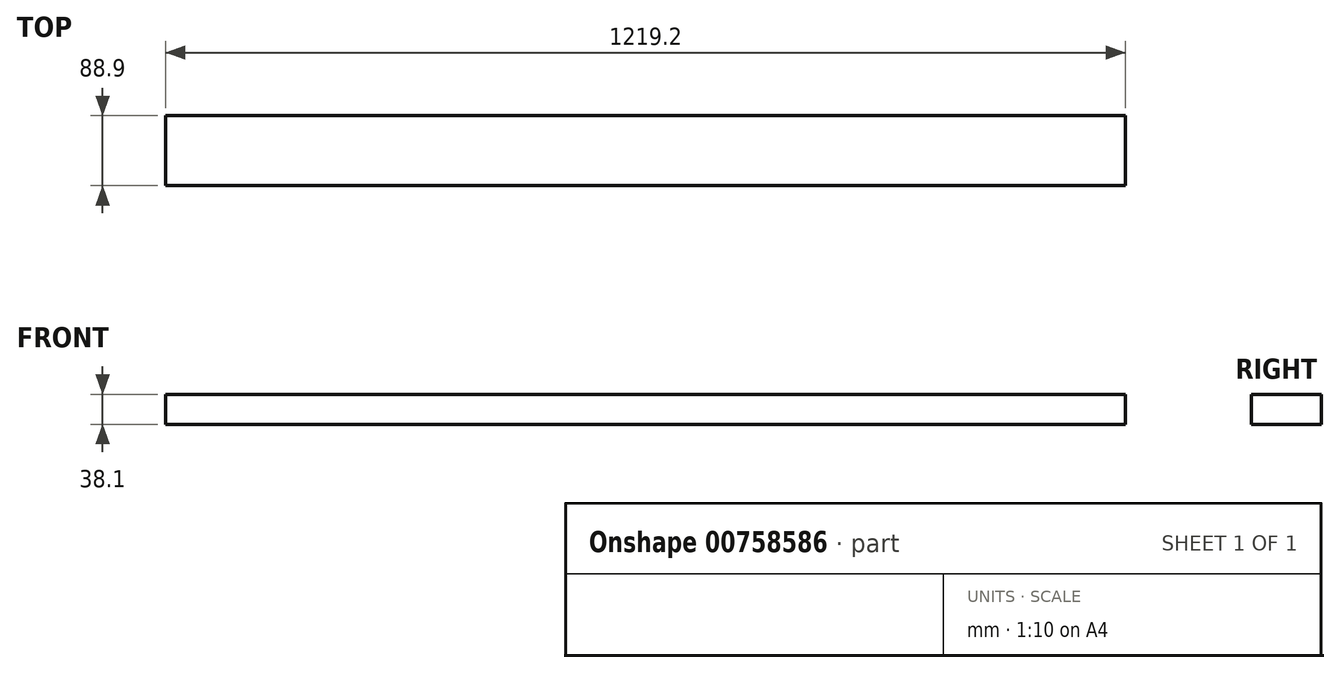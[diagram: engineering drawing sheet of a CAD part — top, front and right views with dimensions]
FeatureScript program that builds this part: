
annotation { "Feature Type Name" : "Feature", "Feature Type Description" : "" }
export const myFeature = defineFeature(function(context is Context, id is Id, definition is map)
    precondition{}
    {
        {
            var Q0;
            Q0=qCreatedBy(makeId("Top.planeOp"),FACE);
            var sketch = newSketch(context, id + "F0", { "sketchPlane" : qUnion([Q0])});
            skLineSegment(sketch, "E0.bottom", {"start": v(-609.6, 44.45) * mm, "end": v(609.6, 44.45) * mm});
            skLineSegment(sketch, "E0.top", {"start": v(-609.6, -44.45) * mm, "end": v(609.6, -44.45) * mm});
            skLineSegment(sketch, "E0.left", {"start": v(-609.6, 44.45) * mm, "end": v(-609.6, -44.45) * mm});
            skLineSegment(sketch, "E0.right", {"start": v(609.6, 44.45) * mm, "end": v(609.6, -44.45) * mm});
            skPoint(sketch, "E0.middle", {"position": v(0, 0) * mm});
            skSolve(sketch);
        }
        {
            var Q0;
            Q0=makeQuery(id+"F0.imprint","IMPRINT",FACE,{"disambiguationData":[TD([[makeQuery(id+"F0.imprint","IMPRINT",EDGE,{"derivedFrom":sQuery(id+"F0.wireOp",EDGE,"E0.bottom")}),-1.0]])]});
            extrude(context, id + "F1", {"entities" : qUnion([Q0]), "depth" : 38.1 * mm, "offsetDistance" : 25.4 * mm});
        }
    });
